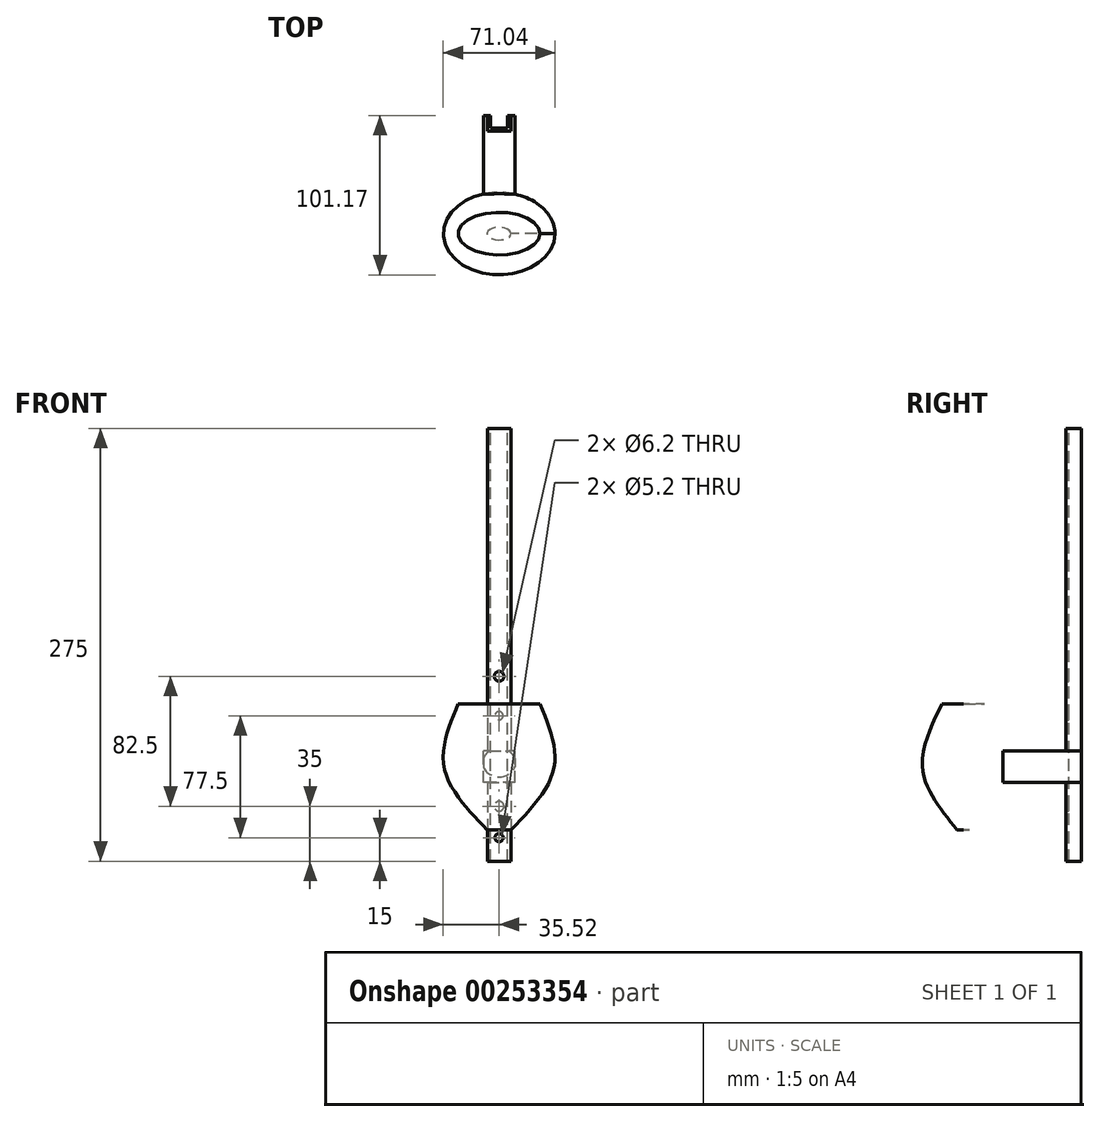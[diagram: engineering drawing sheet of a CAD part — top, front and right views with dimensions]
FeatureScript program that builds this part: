
annotation { "Feature Type Name" : "Feature", "Feature Type Description" : "" }
export const myFeature = defineFeature(function(context is Context, id is Id, definition is map)
    precondition{}
    {
        {
            var Q0;
            Q0=qCreatedBy(makeId("Front.planeOp"),FACE);
            var sketch = newSketch(context, id + "F0", { "sketchPlane" : qUnion([Q0])});
            skLineSegment(sketch, "E0.bottom", {"start": v(0, 275) * mm, "end": v(15, 275) * mm});
            skLineSegment(sketch, "E0.top", {"start": v(0, 0) * mm, "end": v(15, 0) * mm});
            skLineSegment(sketch, "E0.left", {"start": v(0, 275) * mm, "end": v(0, 0) * mm});
            skLineSegment(sketch, "E0.right", {"start": v(15, 275) * mm, "end": v(15, 0) * mm});
            skLineSegment(sketch, "E1", {"start": v(0, 15) * mm, "end": v(15, 15) * mm, "construction": true});
            skLineSegment(sketch, "E2", {"start": v(0, 60) * mm, "end": v(15, 60) * mm, "construction": true});
            skLineSegment(sketch, "E3", {"start": v(0, 35) * mm, "end": v(15, 35) * mm, "construction": true});
            skLineSegment(sketch, "E4", {"start": v(0, 92.5) * mm, "end": v(15, 92.5) * mm, "construction": true});
            skLineSegment(sketch, "E5", {"start": v(0, 117.5) * mm, "end": v(15, 117.5) * mm, "construction": true});
            skCircle(sketch, "E6", {"center": v(7.5, 15) * mm, "radius": 2.6 * mm});
            skCircle(sketch, "E7", {"center": v(7.5, 35) * mm, "radius": 3.1 * mm});
            skCircle(sketch, "E8", {"center": v(7.5, 60) * mm, "radius": 2.6 * mm});
            skCircle(sketch, "E9", {"center": v(7.5, 92.5) * mm, "radius": 2.6 * mm});
            skCircle(sketch, "E10", {"center": v(7.5, 117.5) * mm, "radius": 3.1 * mm});
            skLineSegment(sketch, "E11.bottom", {"start": v(17.5, 50) * mm, "end": v(-2.5, 50) * mm});
            skLineSegment(sketch, "E11.top", {"start": v(17.5, 70) * mm, "end": v(-2.5, 70) * mm});
            skLineSegment(sketch, "E11.left", {"start": v(17.5, 50) * mm, "end": v(17.5, 70) * mm});
            skLineSegment(sketch, "E11.right", {"start": v(-2.5, 50) * mm, "end": v(-2.5, 70) * mm});
            skSolve(sketch);
        }
        {
            var Q0;
            Q0=makeQuery(id+"F0.imprint","IMPRINT",FACE,{"disambiguationData":[TD([[makeQuery(id+"F0.imprint","IMPRINT",EDGE,{"derivedFrom":sQuery(id+"F0.wireOp",EDGE,"E0.bottom")}),-1.0]])]});
            var Q1;
            Q1=makeQuery(id+"F0.imprint","IMPRINT",FACE,{"disambiguationData":[TD([[makeQuery(id+"F0.imprint","IMPRINT",EDGE,{"derivedFrom":sQuery(id+"F0.wireOp",EDGE,"E8")}),-1.0]])]});
            var Q2;
            {var subQ0=sQuery(id+"F0.wireOp",EDGE,"E0.top");Q2=makeQuery(id+"F0.imprint","IMPRINT",FACE,{"disambiguationData":[TD([[makeQuery(id+"F0.imprint","IMPRINT",EDGE,{"derivedFrom":subQ0}),1.0]])]});}
            extrude(context, id + "F1", {"entities" : qUnion([Q0, Q1, Q2]), "depth" : 10 * mm});
        }
        {
            var Q0;
            {var subQ5=sQuery(id+"F0.wireOp",EDGE,"E11.right");Q0=makeQuery(id+"F0.imprint","IMPRINT",FACE,{"disambiguationData":[TD([[makeQuery(id+"F0.imprint","IMPRINT",EDGE,{"derivedFrom":subQ5}),-1.0]])]});}
            var Q1;
            {var subQ5=sQuery(id+"F0.wireOp",EDGE,"E11.left");Q1=makeQuery(id+"F0.imprint","IMPRINT",FACE,{"disambiguationData":[TD([[makeQuery(id+"F0.imprint","IMPRINT",EDGE,{"derivedFrom":subQ5}),1.0]])]});}
            var Q2;
            Q2=makeQuery(id+"F0.imprint","IMPRINT",FACE,{"disambiguationData":[TD([[makeQuery(id+"F0.imprint","IMPRINT",EDGE,{"derivedFrom":sQuery(id+"F0.wireOp",EDGE,"E8")}),-1.0]])]});
            var Q3;
            Q3=makeQuery(id+"F0.imprint","IMPRINT",FACE,{"disambiguationData":[TD([[makeQuery(id+"F0.imprint","IMPRINT",EDGE,{"derivedFrom":sQuery(id+"F0.wireOp",EDGE,"E8")}),1.0]])]});
            extrude(context, id + "F2", {"entities" : qUnion([Q0, Q1, Q2, Q3]), "operationType" : NewBodyOperationType.ADD, "depth" : 50 * mm});
        }
        {
            var Q0;
            Q0=makeQuery(id+"F1.opExtrude","SWEPT_FACE",FACE,{"disambiguationData":[OSD([sQuery(id+"F0.wireOp",EDGE,"E0.bottom")])]});
            var sketch = newSketch(context, id + "F3", { "sketchPlane" : qUnion([Q0])});
            skLineSegment(sketch, "E12.bottom", {"start": v(2, 0) * mm, "end": v(13, 0) * mm});
            skLineSegment(sketch, "E12.top", {"start": v(2, -8) * mm, "end": v(13, -8) * mm});
            skLineSegment(sketch, "E12.left", {"start": v(2, 0) * mm, "end": v(2, -8) * mm});
            skLineSegment(sketch, "E12.right", {"start": v(13, 0) * mm, "end": v(13, -8) * mm});
            skSolve(sketch);
        }
        {
            var Q0;
            Q0=makeQuery(id+"F3.imprint","IMPRINT",FACE,{"disambiguationData":[TD([[makeQuery(id+"F3.imprint","IMPRINT",EDGE,{"derivedFrom":sQuery(id+"F3.wireOp",EDGE,"E12.bottom")}),-1.0]])]});
            extrude(context, id + "F4", {"entities" : qUnion([Q0]), "operationType" : NewBodyOperationType.REMOVE, "oppositeDirection" : true, "depth" : 275 * mm});
        }
        {
            var Q0;
            Q0=makeQuery(id+"F2.opExtrude","SWEPT_FACE",FACE,{"disambiguationData":[OSD([sQuery(id+"F0.wireOp",EDGE,"E11.top")])]});
            cPlane(context, id + "F5", {"entities" : qUnion([Q0]), "cplaneType" : CPlaneType.OFFSET, "offset" : 10 * mm, "oppositeDirection" : true, "width" : 150 * mm, "height" : 150 * mm});
        }
        {
            var Q0;
            Q0=qCreatedBy(id+"F5.planeOp",FACE);
            var sketch = newSketch(context, id + "F6", { "sketchPlane" : qUnion([Q0])});
            skLineSegment(sketch, "E13.0", {"start": v(17.5, -50) * mm, "end": v(-2.5, -50) * mm, "construction": true});
            skLineSegment(sketch, "E14", {"start": v(7.5, -50) * mm, "end": v(7.5, -75) * mm, "construction": true});
            skEllipse(sketch, "E15", {"center": v(7.5, -75) * mm, "majorRadius": 35 * mm, "minorRadius": 26.09 * mm, "majorAxis": v(1, 0)});
            skSolve(sketch);
        }
        {
            var Q0;
            Q0=makeQuery(id+"F2.opExtrude","SWEPT_FACE",FACE,{"disambiguationData":[OSD([sQuery(id+"F0.wireOp",EDGE,"E11.top")])]});
            cPlane(context, id + "F7", {"entities" : qUnion([Q0]), "cplaneType" : CPlaneType.OFFSET, "offset" : 30 * mm, "width" : 150 * mm, "height" : 150 * mm});
        }
        {
            var Q0;
            Q0=qCreatedBy(id+"F7.planeOp",FACE);
            var sketch = newSketch(context, id + "F8", { "sketchPlane" : qUnion([Q0])});
            skPoint(sketch, "E16.0", {"position": v(7.5, -75) * mm});
            skEllipse(sketch, "E17", {"center": v(7.5, -75) * mm, "majorRadius": 26 * mm, "minorRadius": 13.54 * mm, "majorAxis": v(1, 0)});
            skSolve(sketch);
        }
        {
            var Q0;
            Q0=makeQuery(id+"F2.opExtrude","SWEPT_FACE",FACE,{"disambiguationData":[OSD([sQuery(id+"F0.wireOp",EDGE,"E11.top")])]});
            cPlane(context, id + "F9", {"entities" : qUnion([Q0]), "cplaneType" : CPlaneType.OFFSET, "offset" : 50 * mm, "oppositeDirection" : true, "width" : 150 * mm, "height" : 150 * mm});
        }
        {
            var Q0;
            Q0=qCreatedBy(id+"F9.planeOp",FACE);
            var sketch = newSketch(context, id + "F10", { "sketchPlane" : qUnion([Q0])});
            skEllipse(sketch, "E18.0", {"center": v(7.5, -75) * mm, "majorRadius": 7.59 * mm, "minorRadius": 3.95 * mm, "majorAxis": v(1, 0)});
            skSolve(sketch);
        }
        {
            var Q1;
            Q1=makeQuery(id+"F8.imprint","IMPRINT",FACE,{"disambiguationData":[TD([[makeQuery(id+"F8.imprint","IMPRINT",EDGE,{"derivedFrom":sQuery(id+"F8.wireOp",EDGE,"E17")}),1.0]])]});
            var Q2;
            Q2=makeQuery(id+"F6.imprint","IMPRINT",FACE,{"disambiguationData":[TD([[makeQuery(id+"F6.imprint","IMPRINT",EDGE,{"derivedFrom":sQuery(id+"F6.wireOp",EDGE,"E15")}),1.0]])]});
            var Q3;
            Q3=makeQuery(id+"F10.imprint","IMPRINT",FACE,{"disambiguationData":[TD([[makeQuery(id+"F10.imprint","IMPRINT",EDGE,{"derivedFrom":sQuery(id+"F10.wireOp",EDGE,"E18.0")}),1.0]])]});
            loft(context, id + "F11", {"operationType" : NewBodyOperationType.ADD, "sheetProfilesArray" : [{ "sheetProfileEntities" : qUnion([Q1]) }, { "sheetProfileEntities" : qUnion([Q2]) }, { "sheetProfileEntities" : qUnion([Q3]) }]});
        }
    });
